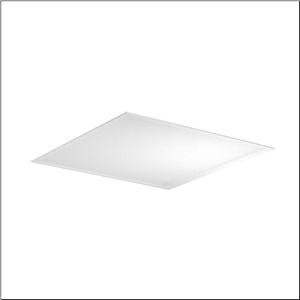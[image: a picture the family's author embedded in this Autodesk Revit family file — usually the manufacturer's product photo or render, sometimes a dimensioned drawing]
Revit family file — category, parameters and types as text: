
# Revit family: apollon_r__31_square_51mp12w72442_a98a
name_source: partatom
category: Lighting Fixtures
units: mm (PartAtom-declared; Revit-internal decimal feet)

## family parameters
Cut with Voids When Loaded = No
Host = Face
Light Source = No
Part Type = Normal
Room Calculation Point = No
Round Connector Dimension = Use Diameter
Shared = No

## types (1)
- Apollon® 31 square (1 x LED, 4000 lm, 27.5 W, 4000K)
    Apparent Load = 28 VA
    CIE Flux Codes = 61 87 97 100 100
    Color Rendering = 80
    Color Temperature = 4000K
    Default Elevation = 1800 mm
    Description = Apollon® 31 square, office luminaire, primary optical cover: micro prismatic cover, of PMMA, CAT 2 (L<= 3000cd/m²), light emission: direct distribution, primary light characteristic: symmetric, installation type: lay-in mounting, LED, rated luminous flux: 4.000lm, luminous efficacy: 145lm/W, light colour: 840, colour temperature: 4000K, with terminal, 3-pole, mains connection: 220..240V, AC, 50/60Hz, rated input power: 28W, housing, of aluminium, traffic white (RAL 9016), module: M600, length: 595mm, width: 595mm, height: 32mm, housing upper side, of sheet steel, galvanised, protection rating (complete): IP20, protection rating (on room side): IP40, insulation class (complete): insulation class II (safety insulation), certification: CE, ENEC, impact resistance: IK03, permissible operating ambient temperature: -20..+40°C, permissible storage temperature: -20..+60°C, packaging unit: 1 piece
    Height = 0 mm  [stored 0 ft]
    Lamp = 1 x LED
    Lamp Light Flux = 4000 lm
    Lamp Power = 27.5 W
    Lamp count = 1
    Length = 595 mm
    Luminous efficacy = 145 lm/W
    Manufacturer = Siteco
    ModVariant = No
    Model = 51MP12W72442
    Mounting Place = Ceiling
    Mounting Type = Recessed
    Number of Poles = 1
    OnlyDefault = Yes
    Power Factor = 1
    Product Name = Apollon® 31 square
    Product group = office luminaire | ceiling recessed
    ProductGroupID = 401
    Protection Class = Protection class II
    Protection Degree = IP 20
    RLX_Detail_Level = 1
    RLX_Emergency_Light_Flux = 0 lm
    RLX_Emergency_Type = 0
    RLX_Emergency_Type_DB = No
    RlxData = <blob elided: 12489 chars, md5=027867dd>
    Socket = socket
    Standby Power = 0 W
    System Light Flux = 4000 lm
    System Power = 28 W
    Type Comments = Product without accessories
    Type Image = l_1291035.jpg
    URL = http://relux.com
    VarID = ---
    Voltage = 0 V
    Weight = 0.00 kg
    Width = 595 mm

note: [stored X ft] marks values corroborated as IEEE doubles in the binary element streams (Revit-internal decimal feet)

## geometry (parser evidence)
native form markers: Sweep x10
no freeform markers — native parametric forms only
